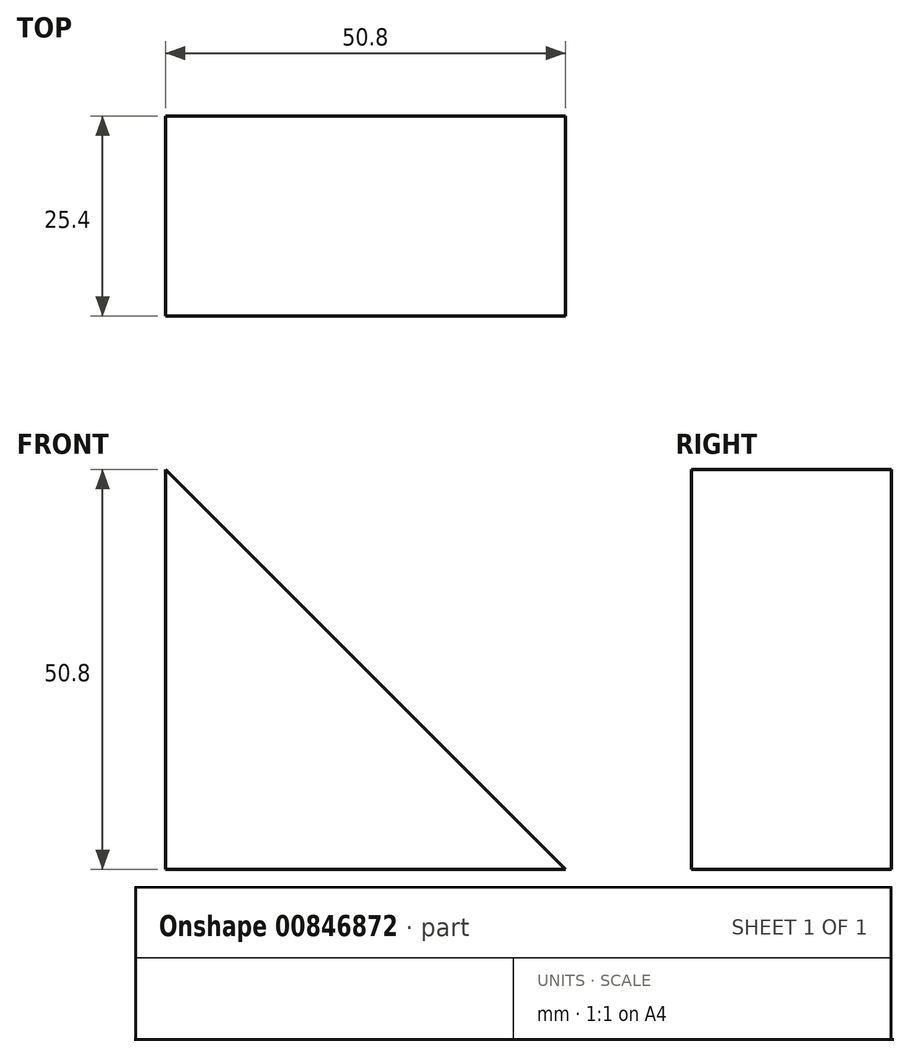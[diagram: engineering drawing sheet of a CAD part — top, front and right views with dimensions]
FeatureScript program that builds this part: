
annotation { "Feature Type Name" : "Feature", "Feature Type Description" : "" }
export const myFeature = defineFeature(function(context is Context, id is Id, definition is map)
    precondition{}
    {
        {
            var Q0;
            Q0=qCreatedBy(makeId("Front.planeOp"),FACE);
            var sketch = newSketch(context, id + "F0", { "sketchPlane" : qUnion([Q0])});
            skLineSegment(sketch, "E0", {"start": v(0, 0) * mm, "end": v(-50.8, 0) * mm});
            skLineSegment(sketch, "E1", {"start": v(-50.8, 0) * mm, "end": v(-50.8, 50.8) * mm});
            skLineSegment(sketch, "E2", {"start": v(-50.8, 50.8) * mm, "end": v(0, 0) * mm});
            skSolve(sketch);
        }
        {
            var Q0;
            Q0=qSketchRegion(id+"F0",true);
            extrude(context, id + "F1", {"entities" : qUnion([Q0]), "depth" : 25.4 * mm, "offsetDistance" : 25.4 * mm});
        }
    });
